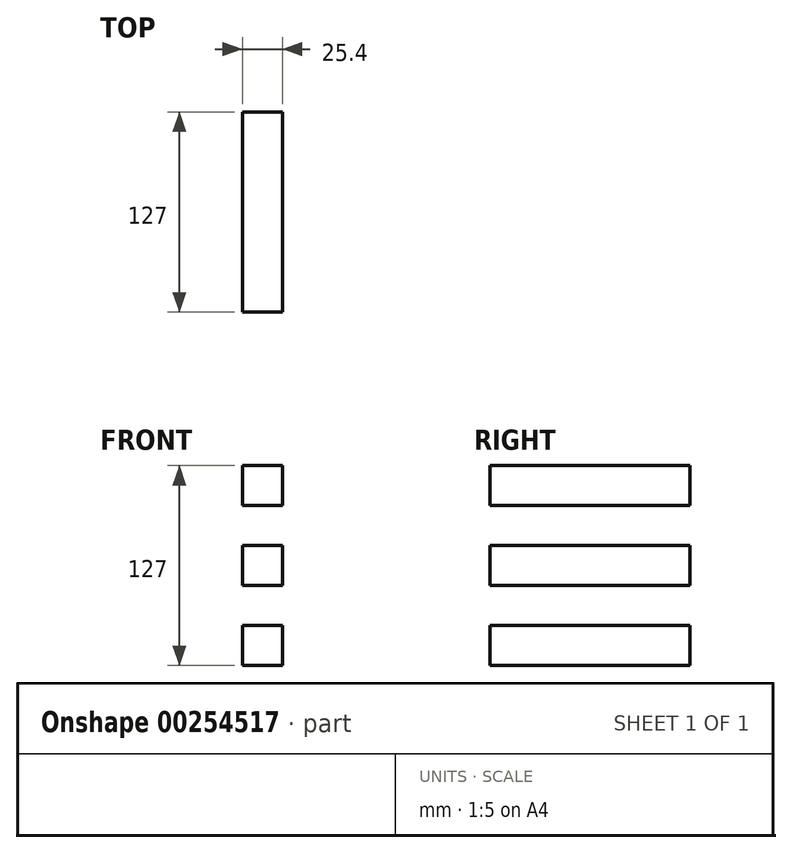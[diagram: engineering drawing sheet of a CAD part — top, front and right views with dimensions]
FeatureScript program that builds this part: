
annotation { "Feature Type Name" : "Feature", "Feature Type Description" : "" }
export const myFeature = defineFeature(function(context is Context, id is Id, definition is map)
    precondition{}
    {
        {
            var Q0;
            Q0=qCreatedBy(makeId("Front.planeOp"),FACE);
            var sketch = newSketch(context, id + "F0", { "sketchPlane" : qUnion([Q0])});
            skLineSegment(sketch, "E0.bottom", {"start": v(12.7, 12.7) * mm, "end": v(-12.7, 12.7) * mm});
            skLineSegment(sketch, "E0.top", {"start": v(12.7, -12.7) * mm, "end": v(-12.7, -12.7) * mm});
            skLineSegment(sketch, "E0.left", {"start": v(12.7, 12.7) * mm, "end": v(12.7, -12.7) * mm});
            skLineSegment(sketch, "E0.right", {"start": v(-12.7, 12.7) * mm, "end": v(-12.7, -12.7) * mm});
            skPoint(sketch, "E0.middle", {"position": v(0, 0) * mm});
            skLineSegment(sketch, "E1", {"start": v(0, 0) * mm, "end": v(0, 50.8) * mm});
            skPoint(sketch, "E1.endSnap0", {"position": v(0, 12.7) * mm});
            skLineSegment(sketch, "E2.bottom", {"start": v(12.7, 63.5) * mm, "end": v(-12.7, 63.5) * mm});
            skLineSegment(sketch, "E2.top", {"start": v(12.7, 38.1) * mm, "end": v(-12.7, 38.1) * mm});
            skLineSegment(sketch, "E2.left", {"start": v(12.7, 63.5) * mm, "end": v(12.7, 38.1) * mm});
            skLineSegment(sketch, "E2.right", {"start": v(-12.7, 63.5) * mm, "end": v(-12.7, 38.1) * mm});
            skPoint(sketch, "E2.middle", {"position": v(0, 50.8) * mm});
            skLineSegment(sketch, "E3", {"start": v(0, 0) * mm, "end": v(0, -50.8) * mm});
            skLineSegment(sketch, "E4.bottom", {"start": v(12.7, -38.1) * mm, "end": v(-12.7, -38.1) * mm});
            skLineSegment(sketch, "E4.top", {"start": v(12.7, -63.5) * mm, "end": v(-12.7, -63.5) * mm});
            skLineSegment(sketch, "E4.left", {"start": v(12.7, -38.1) * mm, "end": v(12.7, -63.5) * mm});
            skLineSegment(sketch, "E4.right", {"start": v(-12.7, -38.1) * mm, "end": v(-12.7, -63.5) * mm});
            skPoint(sketch, "E4.middle", {"position": v(0, -50.8) * mm});
            skSolve(sketch);
        }
        {
            var Q0;
            Q0=makeQuery(id+"F0.imprint","IMPRINT",FACE,{"disambiguationData":[TD([[makeQuery(id+"F0.imprint","IMPRINT",EDGE,{"derivedFrom":sQuery(id+"F0.wireOp",EDGE,"E2.bottom")}),1.0]])]});
            var Q1;
            {var subQ5=sQuery(id+"F0.wireOp",EDGE,"E0.left");Q1=makeQuery(id+"F0.imprint","IMPRINT",FACE,{"disambiguationData":[TD([[makeQuery(id+"F0.imprint","IMPRINT",EDGE,{"derivedFrom":subQ5}),-1.0]])]});}
            var Q2;
            {var subQ5=sQuery(id+"F0.wireOp",EDGE,"E0.right");Q2=makeQuery(id+"F0.imprint","IMPRINT",FACE,{"disambiguationData":[TD([[makeQuery(id+"F0.imprint","IMPRINT",EDGE,{"derivedFrom":subQ5}),1.0]])]});}
            var Q3;
            Q3=makeQuery(id+"F0.imprint","IMPRINT",FACE,{"disambiguationData":[TD([[makeQuery(id+"F0.imprint","IMPRINT",EDGE,{"derivedFrom":sQuery(id+"F0.wireOp",EDGE,"E4.top")}),-1.0]])]});
            extrude(context, id + "F1", {"entities" : qUnion([Q0, Q1, Q2, Q3]), "endBound" : BoundingType.SYMMETRIC, "depth" : 127 * mm});
        }
    });
